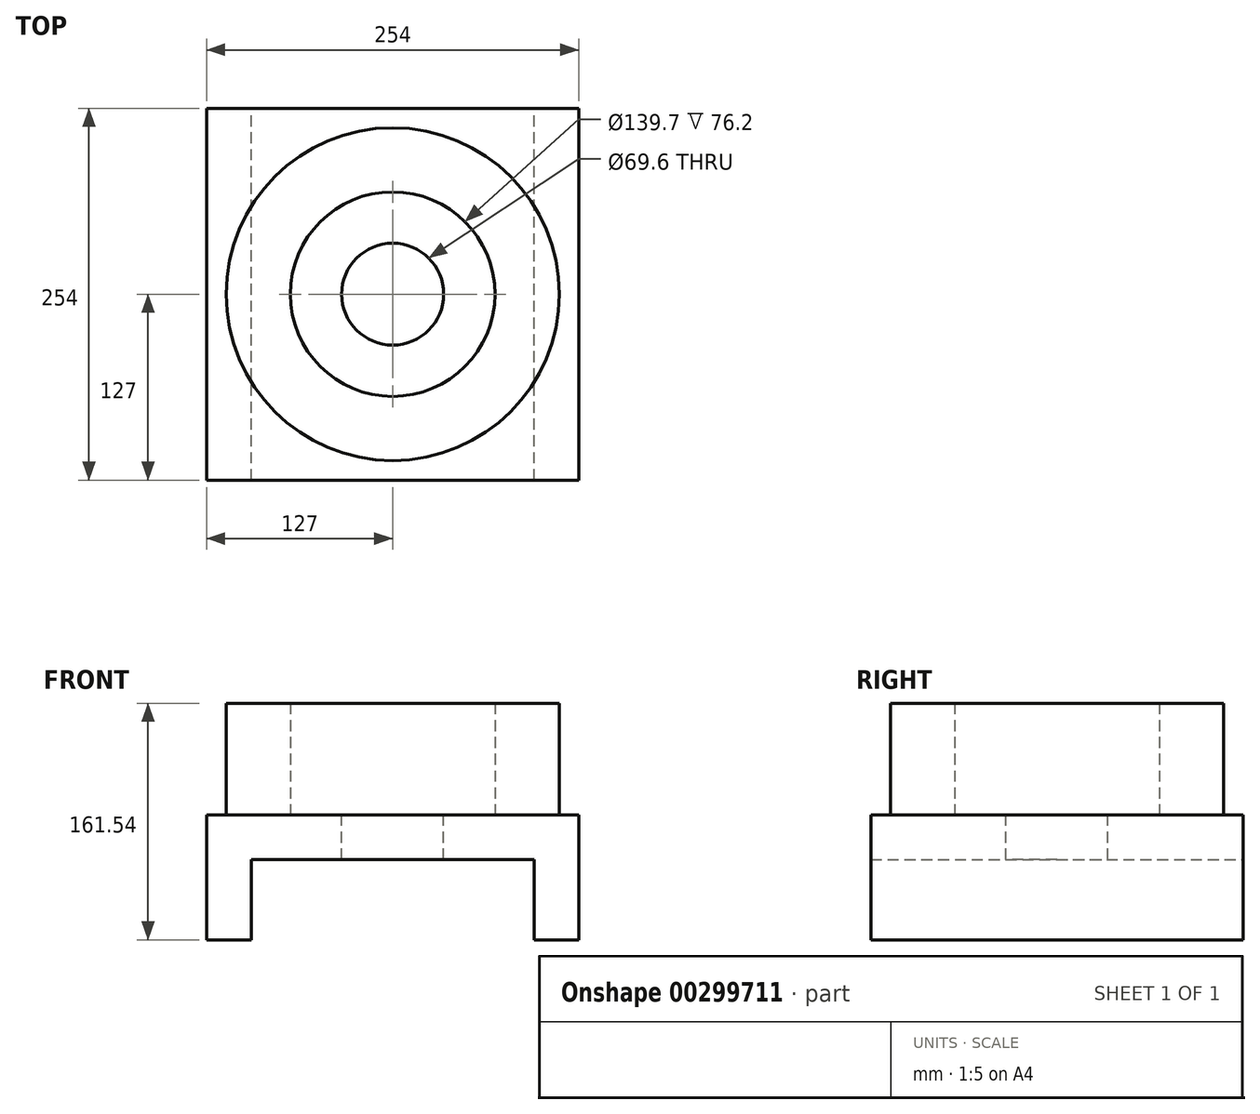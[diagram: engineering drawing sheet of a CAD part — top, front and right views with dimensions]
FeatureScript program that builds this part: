
annotation { "Feature Type Name" : "Feature", "Feature Type Description" : "" }
export const myFeature = defineFeature(function(context is Context, id is Id, definition is map)
    precondition{}
    {
        {
            var Q0;
            Q0=qCreatedBy(makeId("Front.planeOp"),FACE);
            var sketch = newSketch(context, id + "F0", { "sketchPlane" : qUnion([Q0])});
            skLineSegment(sketch, "E0", {"start": v(0, 0) * mm, "end": v(127, 0) * mm});
            skLineSegment(sketch, "E1", {"start": v(127, 0) * mm, "end": v(127, -85.34) * mm});
            skLineSegment(sketch, "E2", {"start": v(127, -85.34) * mm, "end": v(96.52, -85.34) * mm});
            skLineSegment(sketch, "E3", {"start": v(96.52, -85.34) * mm, "end": v(96.52, -30.48) * mm});
            skLineSegment(sketch, "E4", {"start": v(96.52, -30.48) * mm, "end": v(0, -30.48) * mm});
            skLineSegment(sketch, "E5", {"start": v(0, -30.48) * mm, "end": v(0, 0) * mm});
            skLineSegment(sketch, "E6.MirrorCS", {"start": v(0, 0) * mm, "end": v(-127, 0) * mm});
            skLineSegment(sketch, "E7.MirrorCS", {"start": v(-127, 0) * mm, "end": v(-127, -85.34) * mm});
            skLineSegment(sketch, "E8.MirrorCS", {"start": v(-127, -85.34) * mm, "end": v(-96.52, -85.34) * mm});
            skLineSegment(sketch, "E9.MirrorCS", {"start": v(-96.52, -85.34) * mm, "end": v(-96.52, -30.48) * mm});
            skLineSegment(sketch, "E10.MirrorCS", {"start": v(-96.52, -30.48) * mm, "end": v(0, -30.48) * mm});
            skSolve(sketch);
        }
        {
            var Q0;
            Q0 = qSketchRegion(id + "F0", true);
            extrude(context, id + "F1", {"entities" : qUnion([Q0]), "endBound" : BoundingType.SYMMETRIC, "depth" : 254 * mm});
        }
        {
            var Q0;
            Q0=makeQuery(id+"F1.opExtrude","SWEPT_FACE",FACE,{"disambiguationData":[OSD([sQuery(id+"F0.wireOp",EDGE,"E0"),sQuery(id+"F0.wireOp",EDGE,"E6.MirrorCS")])]});
            var sketch = newSketch(context, id + "F2", { "sketchPlane" : qUnion([Q0])});
            skCircle(sketch, "E11", {"center": v(0, 0) * mm, "radius": 34.8 * mm});
            skCircle(sketch, "E12", {"center": v(0, 0) * mm, "radius": 69.85 * mm});
            skCircle(sketch, "E13", {"center": v(0, 0) * mm, "radius": 113.67 * mm});
            skSolve(sketch);
        }
        {
            var Q0;
            Q0 = qSketchRegion(id + "F2", true);
            extrude(context, id + "F3", {"entities" : qUnion([Q0]), "operationType" : NewBodyOperationType.ADD, "depth" : 76.2 * mm});
        }
        {
            var Q0;
            Q0=makeQuery(id+"F2.imprint","IMPRINT",FACE,{"disambiguationData":[TD([[makeQuery(id+"F2.imprint","IMPRINT",EDGE,{"derivedFrom":sQuery(id+"F2.wireOp",EDGE,"E11")}),1.0]])]});
            extrude(context, id + "F4", {"entities" : qUnion([Q0]), "operationType" : NewBodyOperationType.REMOVE, "oppositeDirection" : true, "depth" : 101.6 * mm});
        }
    });
